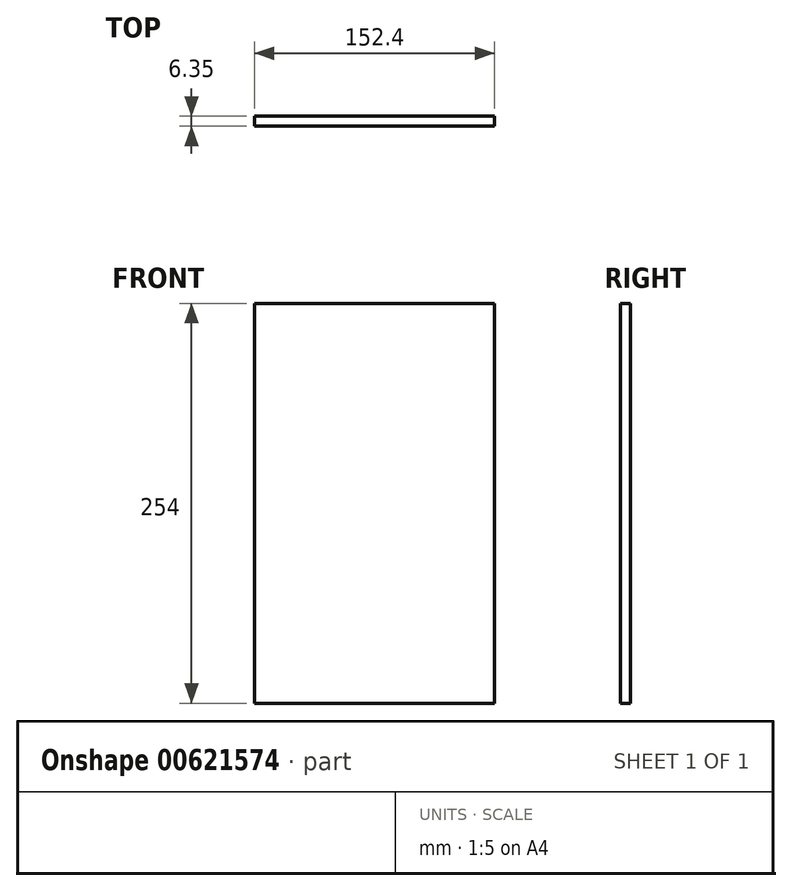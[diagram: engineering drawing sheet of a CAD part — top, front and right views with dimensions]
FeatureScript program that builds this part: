
annotation { "Feature Type Name" : "Feature", "Feature Type Description" : "" }
export const myFeature = defineFeature(function(context is Context, id is Id, definition is map)
    precondition{}
    {
        {
            var Q0;
            Q0=qCreatedBy(makeId("Front.planeOp"),FACE);
            var sketch = newSketch(context, id + "F0", { "sketchPlane" : qUnion([Q0])});
            skLineSegment(sketch, "E0.bottom", {"start": v(76.2, 127) * mm, "end": v(-76.2, 127) * mm});
            skLineSegment(sketch, "E0.top", {"start": v(76.2, -127) * mm, "end": v(-76.2, -127) * mm});
            skLineSegment(sketch, "E0.left", {"start": v(76.2, 127) * mm, "end": v(76.2, -127) * mm});
            skLineSegment(sketch, "E0.right", {"start": v(-76.2, 127) * mm, "end": v(-76.2, -127) * mm});
            skPoint(sketch, "E0.middle", {"position": v(0, 0) * mm});
            skSolve(sketch);
        }
        {
            var Q0;
            Q0 = qSketchRegion(id + "F0", true);
            extrude(context, id + "F1", {"entities" : qUnion([Q0]), "depth" : 6.35 * mm, "offsetDistance" : 25.4 * mm});
        }
    });
